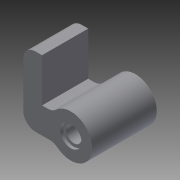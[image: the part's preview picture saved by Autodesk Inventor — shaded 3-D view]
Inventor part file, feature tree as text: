
AUTODESK INVENTOR PART (.ipt)
format: ipt  version: 2015 (Build 190159000, 159)  size: 131,072 bytes
history: native  units: in
note: dims shown in document units (in); Inventor stores cm internally (conversion verified against a paired STEP export)
features: extrude x4, sketch x4, mirror x1, fillet x1, reference x1
ambient origin geometry x8: Origin, YZ Plane, XZ Plane, XY Plane, X Axis, Y Axis, Z Axis, Center Point
bodies: Solid1 (feature_tree)
feature tree (11):
  extrude  "Extrusion1"  Depth=0.9375in TaperAngle=0.0deg
  extrude  "Extrusion2"  Depth=0.4882in TaperAngle=0.0deg
  mirror  "Mirror1"
  extrude  "Extrusion3"  Depth=0.0591in TaperAngle=0.0deg
  extrude  "Extrusion4"  [1 undecoded]
  fillet  "Fillet1"  [1 undecoded]
  sketch  "Sketch1"  dims[d0=0.375in d1=0.0in d2=0.9375in d3=0.0in]
  reference  "Reference1"
  sketch  "Sketch2"  dims[d4=0.3125in d5=0.4882in d6=0.0in]
  sketch  "Sketch3"  dims[d7=0.4331in d8=0.0591in d9=0.0in]
  sketch  "Sketch4"  dims[d10=0.25in]
note: 2 required parameter values undecoded (feature->parameter linkage not recoverable at this tier; creation-order binding heuristic only, values carry confidence <= 0.55)
